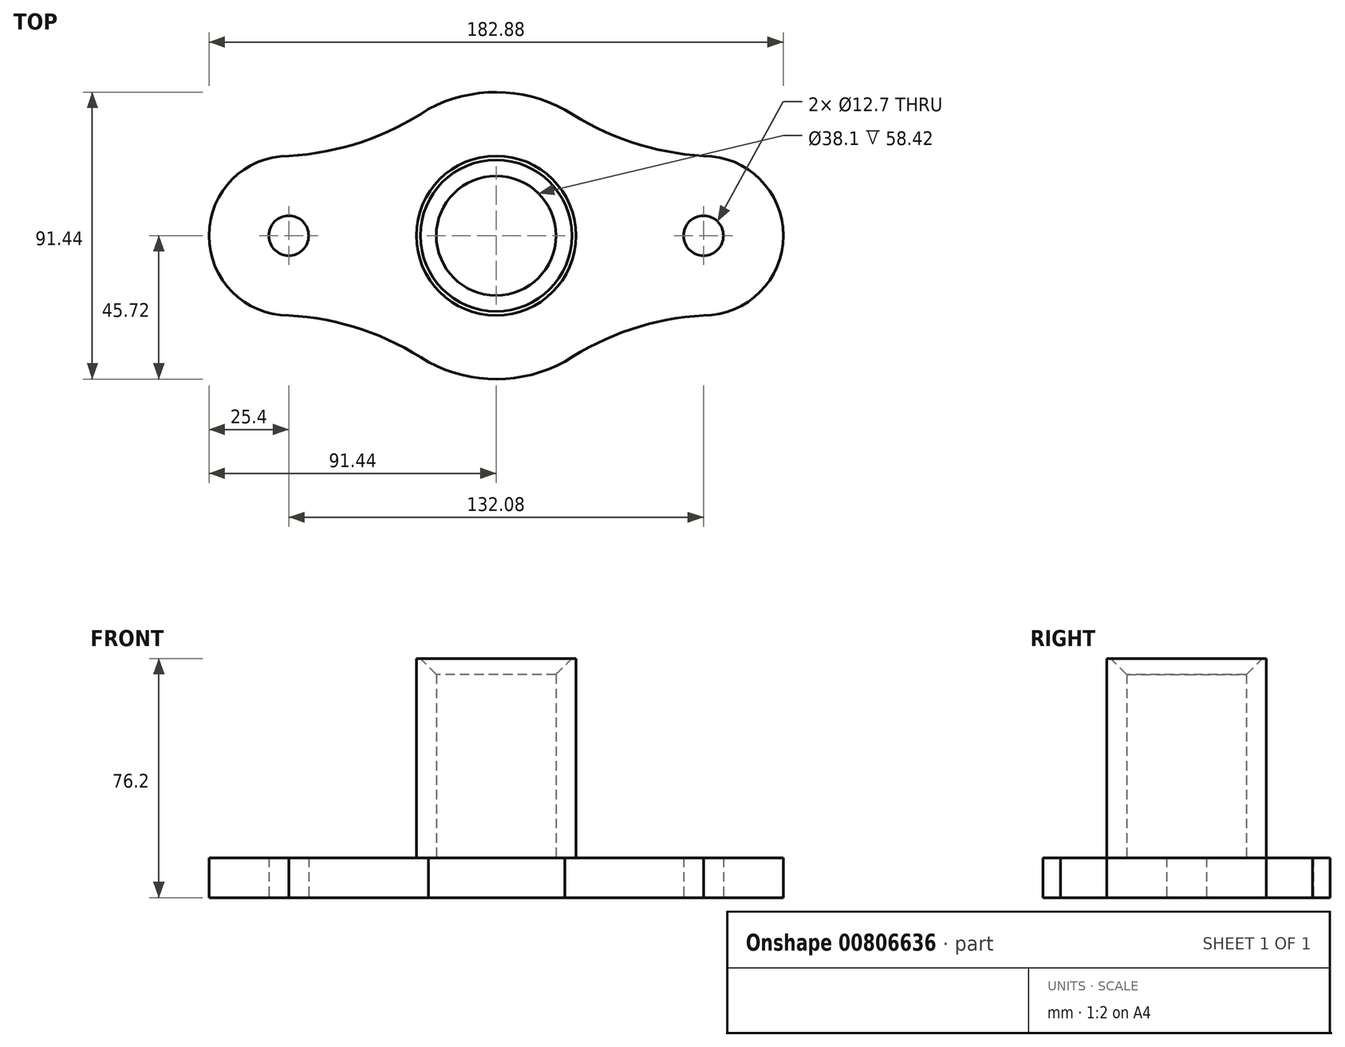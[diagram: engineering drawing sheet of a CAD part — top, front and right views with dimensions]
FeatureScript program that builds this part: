
annotation { "Feature Type Name" : "Feature", "Feature Type Description" : "" }
export const myFeature = defineFeature(function(context is Context, id is Id, definition is map)
    precondition{}
    {
        {
            var Q0;
            Q0=qCreatedBy(makeId("Top.planeOp"),FACE);
            var sketch = newSketch(context, id + "F0", { "sketchPlane" : qUnion([Q0])});
            skArc(sketch, "E0", {"start": v(-21.51, -40.34) * mm, "mid": v(0.23, -45.72) * mm, "end": v(21.91, -40.13) * mm});
            skArc(sketch, "E1", {"start": v(66.04, -25.4) * mm, "mid": v(91.44, 0) * mm, "end": v(66.04, 25.4) * mm});
            skArc(sketch, "E2", {"start": v(-66.04, 25.4) * mm, "mid": v(-91.44, 0) * mm, "end": v(-66.04, -25.4) * mm});
            skArc(sketch, "E3", {"start": v(-21.51, -40.34) * mm, "mid": v(-42.77, -29.88) * mm, "end": v(-66.04, -25.4) * mm});
            skArc(sketch, "E4", {"start": v(-66.04, 25.4) * mm, "mid": v(-42.77, 29.88) * mm, "end": v(-21.51, 40.34) * mm});
            skArc(sketch, "E5", {"start": v(21.91, 40.13) * mm, "mid": v(43, 29.83) * mm, "end": v(66.04, 25.4) * mm});
            skArc(sketch, "E6", {"start": v(66.04, -25.4) * mm, "mid": v(43, -29.83) * mm, "end": v(21.91, -40.13) * mm});
            skCircle(sketch, "E7", {"center": v(-66.04, 0) * mm, "radius": 6.35 * mm});
            skCircle(sketch, "E8", {"center": v(66.04, 0) * mm, "radius": 6.35 * mm});
            skArc(sketch, "E9.trimOffspring", {"start": v(21.91, 40.13) * mm, "mid": v(0.23, 45.72) * mm, "end": v(-21.51, 40.34) * mm});
            skSolve(sketch);
        }
        {
            var Q0;
            Q0=makeQuery(id+"F0.imprint","IMPRINT",FACE,{"disambiguationData":[TD([[makeQuery(id+"F0.imprint","IMPRINT",EDGE,{"derivedFrom":sQuery(id+"F0.wireOp",EDGE,"E0")}),1.0]])]});
            extrude(context, id + "F1", {"entities" : qUnion([Q0]), "depth" : 12.7 * mm, "offsetDistance" : 25.4 * mm});
        }
        {
            var Q0;
            Q0=qCreatedBy(makeId("Top.planeOp"),FACE);
            var sketch = newSketch(context, id + "F2", { "sketchPlane" : qUnion([Q0])});
            skCircle(sketch, "E10", {"center": v(0, 0) * mm, "radius": 25.4 * mm});
            skCircle(sketch, "E11", {"center": v(0, 0) * mm, "radius": 19.05 * mm});
            skSolve(sketch);
        }
        {
            var Q0;
            Q0 = qSketchRegion(id + "F2", true);
            extrude(context, id + "F3", {"entities" : qUnion([Q0]), "operationType" : NewBodyOperationType.ADD, "depth" : 76.2 * mm, "offsetDistance" : 25.4 * mm});
        }
        {
            var Q0;
            Q0=makeQuery(id+"F3.opExtrude","CAP_EDGE",EDGE,{"disambiguationData":[OSD([sQuery(id+"F2.wireOp",EDGE,"E11")])],"isStart":false});
            chamfer(context, id + "F4", {"entities" : qUnion([Q0]), "width" : 5.08 * mm});
        }
    });
